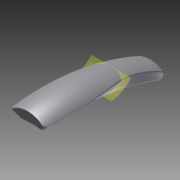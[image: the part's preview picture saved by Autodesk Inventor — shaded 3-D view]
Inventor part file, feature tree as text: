
AUTODESK INVENTOR PART (.ipt)
format: ipt  version: 2011 (Build 150239000, 239)  size: 598,528 bytes
history: native  units: mm (DEFAULTED — no unit token found)
features: other x18, sketch x8, extrude x6, fillet x5, surface_op x4, loft x3, delete_face x1, plane x1, projected_geometry x1, sweep x1
ambient origin geometry x8: Origin, YZ Plane, XZ Plane, XY Plane, X Axis, Y Axis, Z Axis, Center Point
bodies: Solid1 (feature_tree)
feature tree (48):
  other  "Top Curve"
  extrude  "Extrusion1"  Depth=12.7mm
  surface_op  "Replace Face1"
  extrude  "Extrusion2"  Depth=158.75mm
  extrude  "Extrusion3"  TaperAngle=0.0deg  [1 undecoded]
  sketch  "3D Sketch2"
  sketch  "3D Sketch3"
  delete_face  "Delete Face1"
  surface_op  "Stitch Surface5"
  plane  "Work Plane3"
  other  "Slice"
  extrude  "Extrusion11"  Depth=158.75mm
  other  "Work Point1"
  other  "Work Axis1"
  fillet  "Fillet13"  Radius=101.6mm
  fillet  "Fillet14"  Radius=22.225mm
  fillet  "Fillet15"  Radius=22.225mm
  fillet  "Fillet16"  Radius=17.4625mm
  fillet  "Fillet17"  Radius=17.4625mm
  sketch  "Sketch3"  dims[d2=3.175mm d3=12.7mm]
  other  "Srf1"
  sketch  "Sketch5"  dims[d4=50.8mm d10=158.75mm]
  sketch  "Sketch6"  dims[d11=25.4mm d12=0.0mm]
  sketch  "Sketch7"  dims[d13=50.8mm d14=158.75mm d15=101.6mm d16=0.0mm d17=22.225mm d18=22.225mm d19=17.4625mm d20=17.4625mm]
  sketch  "Sketch8"  dims[d21=282.575mm d22=203.2mm]
  other  "Srf2"
  sketch  "Sketch19"  dims[d23=92.075mm d24=101.6mm d25=0.0mm d26=19.05mm d27=15.875mm d28=304.8mm d29=101.6mm d30=0.0mm d32=30.1752mm d33=6.35mm d34=6.35mm d35=63.5mm d36=0.0mm d65=3.490659mm d88=38.1mm d89=82.55mm d90=107.95mm d144=25.4mm d145=0.0mm d151=50.8mm d152=0.0mm d155=7.9502mm d156=7.9502mm d157=0.0mm d158=90.0deg d159=0.0mm d160=90.0deg d161=0.0mm d162=90.0deg d163=0.0mm d164=90.0deg d165=0.0mm d166=90.0deg d167=0.0mm d168=90.0deg d170=3.81mm d171=3.81mm d172=1.27mm d173=3.81mm d174=1.27mm d175=0.254mm]
  projected_geometry  "Projected Loop6"
  other  "Srf8"
  other  "Edges25"
  other  "Srf3"
  other  "Edges26"
  other  "Srf4"
  other  "Edges27"
  other  "Edges28"
  other  "Srf5"
  other  "Srf6"
  other  "Srf7"
  sweep  "SweepSrf3"
  extrude  "ExtrusionSrf1"  Depth=101.6mm TaperAngle=0.0deg
  loft  "LoftSrf9"
  loft  "LoftSrf10"
  loft  "LoftSrf11"
  surface_op  "Boundary Patch1"
  surface_op  "Boundary Patch2"
  extrude  "ExtrusionSrf2"  Depth=101.6mm TaperAngle=0.0deg
  other  "3D Intersection2"
  other  "3D Intersection3"
note: 1 required parameter value undecoded (feature->parameter linkage not recoverable at this tier; creation-order binding heuristic only, values carry confidence <= 0.55)
